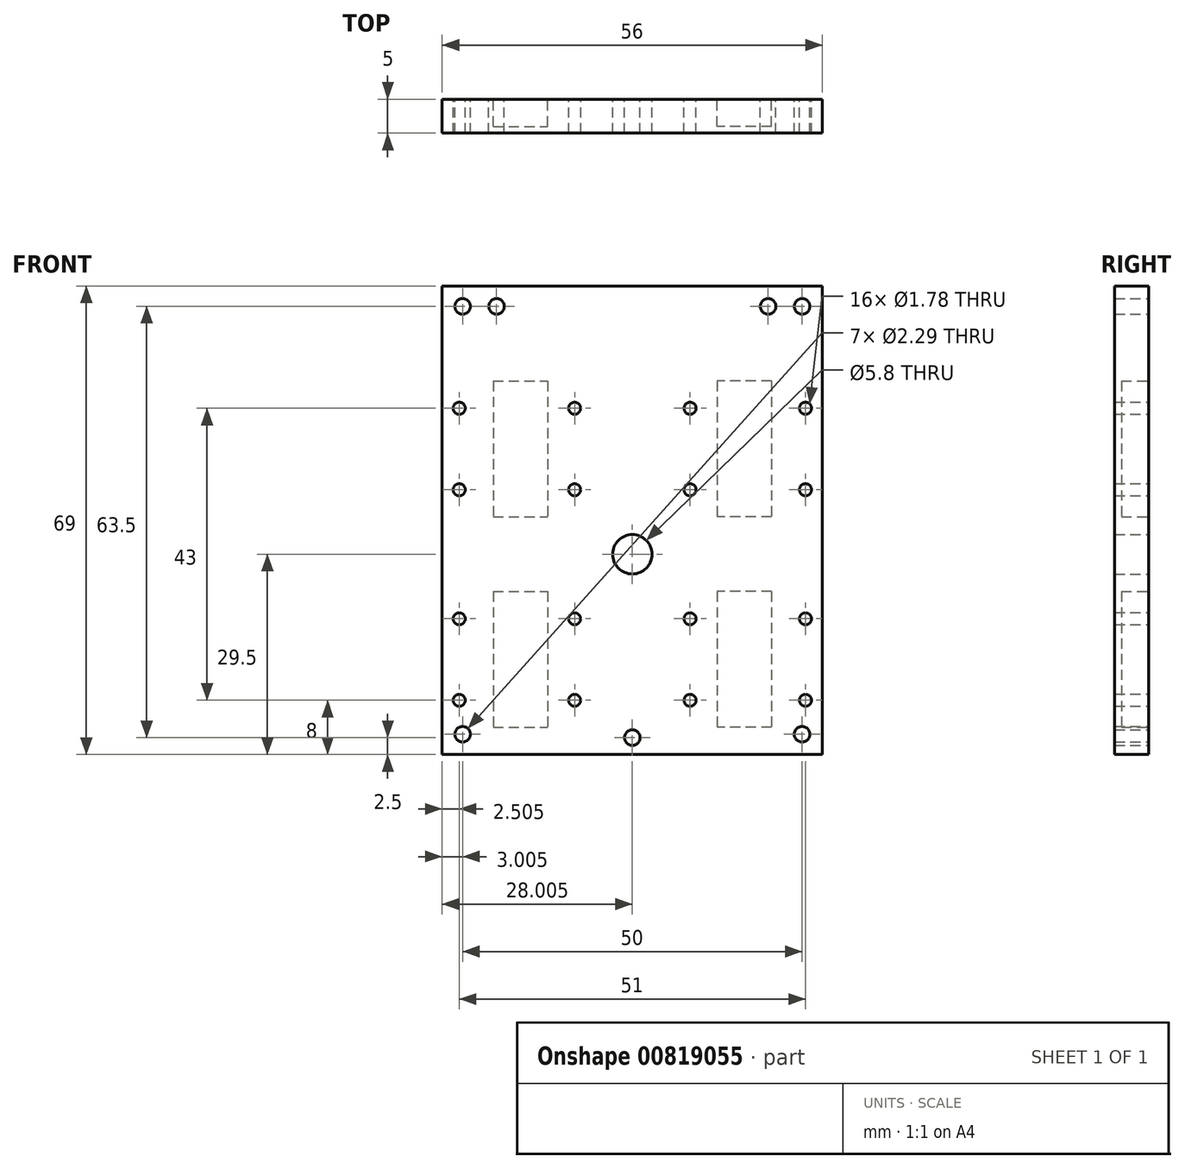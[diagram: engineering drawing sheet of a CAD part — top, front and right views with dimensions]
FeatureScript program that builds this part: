
annotation { "Feature Type Name" : "Feature", "Feature Type Description" : "" }
export const myFeature = defineFeature(function(context is Context, id is Id, definition is map)
    precondition{}
    {
        {
            var Q0;
            Q0=qCreatedBy(makeId("Front.planeOp"),FACE);
            var sketch = newSketch(context, id + "F0", { "sketchPlane" : qUnion([Q0])});
            skCircle(sketch, "E0", {"center": v(-20.38, 33.5) * mm, "radius": 1.14 * mm});
            skCircle(sketch, "E1", {"center": v(-25.88, 18.5) * mm, "radius": 0.89 * mm});
            skCircle(sketch, "E2", {"center": v(-8.88, 18.5) * mm, "radius": 0.89 * mm});
            skCircle(sketch, "E3", {"center": v(-8.88, 6.5) * mm, "radius": 0.89 * mm});
            skCircle(sketch, "E4", {"center": v(-25.88, 6.5) * mm, "radius": 0.89 * mm});
            skCircle(sketch, "E5", {"center": v(-25.87, -12.5) * mm, "radius": 0.89 * mm});
            skCircle(sketch, "E6", {"center": v(-8.88, -12.5) * mm, "radius": 0.89 * mm});
            skCircle(sketch, "E7", {"center": v(-8.88, -24.5) * mm, "radius": 0.89 * mm});
            skCircle(sketch, "E8", {"center": v(-25.87, -24.5) * mm, "radius": 0.89 * mm});
            skCircle(sketch, "E9", {"center": v(-25.38, -29.5) * mm, "radius": 1.14 * mm});
            skCircle(sketch, "E10", {"center": v(-0.38, -30) * mm, "radius": 1.14 * mm});
            skCircle(sketch, "E11", {"center": v(-0.38, -3) * mm, "radius": 2.9 * mm});
            skLineSegment(sketch, "E12", {"start": v(27.62, 36.5) * mm, "end": v(-28.38, 36.5) * mm});
            skLineSegment(sketch, "E13", {"start": v(-28.37, 36.5) * mm, "end": v(-28.38, -32.5) * mm});
            skLineSegment(sketch, "E14", {"start": v(27.63, -32.5) * mm, "end": v(-28.38, -32.5) * mm});
            skLineSegment(sketch, "E15.bottom", {"start": v(-28.38, -32.5) * mm, "end": v(-22.38, -32.5) * mm, "construction": true});
            skLineSegment(sketch, "E15.top", {"start": v(-28.38, -26.5) * mm, "end": v(-22.38, -26.5) * mm, "construction": true});
            skLineSegment(sketch, "E15.left", {"start": v(-28.38, -32.5) * mm, "end": v(-28.38, -26.5) * mm, "construction": true});
            skLineSegment(sketch, "E15.right", {"start": v(-22.38, -32.5) * mm, "end": v(-22.38, -26.5) * mm, "construction": true});
            skLineSegment(sketch, "E16", {"start": v(-28.38, -26.5) * mm, "end": v(-22.38, -32.5) * mm});
            skLineSegment(sketch, "E17", {"start": v(-28.38, -32.5) * mm, "end": v(-22.38, -26.5) * mm});
            skPoint(sketch, "E18", {"position": v(-28.38, 2) * mm});
            skLineSegment(sketch, "E19", {"start": v(-0.38, 36.5) * mm, "end": v(-20.38, 36.5) * mm, "construction": true});
            skLineSegment(sketch, "E20", {"start": v(-20.38, 36.5) * mm, "end": v(-20.38, 33.5) * mm});
            skLineSegment(sketch, "E21", {"start": v(-0.37, -32.5) * mm, "end": v(-0.38, -30) * mm});
            skLineSegment(sketch, "E22", {"start": v(-8.88, -12.5) * mm, "end": v(-8.88, -24.5) * mm, "construction": true});
            skPoint(sketch, "E23", {"position": v(-8.88, -18.5) * mm});
            skLineSegment(sketch, "E24", {"start": v(-8.88, -18.5) * mm, "end": v(-28.37, -18.5) * mm, "construction": true});
            skLineSegment(sketch, "E25", {"start": v(-25.88, -24.5) * mm, "end": v(-25.88, -12.5) * mm, "construction": true});
            skPoint(sketch, "E26", {"position": v(-25.88, -18.5) * mm});
            skPoint(sketch, "E27", {"position": v(-20.88, -18.5) * mm});
            skLineSegment(sketch, "E28", {"start": v(-20.88, -18.5) * mm, "end": v(-20.88, -8.5) * mm, "construction": true});
            skLineSegment(sketch, "E29", {"start": v(-20.88, -8.5) * mm, "end": v(-12.88, -8.5) * mm, "construction": true});
            skLineSegment(sketch, "E30", {"start": v(-12.88, -8.5) * mm, "end": v(-12.88, -28.5) * mm, "construction": true});
            skLineSegment(sketch, "E31.bottom", {"start": v(-20.88, -8.5) * mm, "end": v(-12.88, -8.5) * mm});
            skLineSegment(sketch, "E31.top", {"start": v(-20.88, -28.5) * mm, "end": v(-12.88, -28.5) * mm});
            skLineSegment(sketch, "E31.left", {"start": v(-20.88, -8.5) * mm, "end": v(-20.88, -28.5) * mm});
            skLineSegment(sketch, "E31.right", {"start": v(-12.88, -8.5) * mm, "end": v(-12.88, -28.5) * mm});
            skLineSegment(sketch, "E32", {"start": v(-25.88, 18.5) * mm, "end": v(-25.88, 6.5) * mm, "construction": true});
            skPoint(sketch, "E33", {"position": v(-25.88, 12.5) * mm});
            skLineSegment(sketch, "E34", {"start": v(-8.88, 18.5) * mm, "end": v(-8.88, 6.5) * mm, "construction": true});
            skPoint(sketch, "E35", {"position": v(-8.88, 12.5) * mm});
            skLineSegment(sketch, "E36", {"start": v(-8.88, 12.5) * mm, "end": v(-28.38, 12.5) * mm, "construction": true});
            skLineSegment(sketch, "E37", {"start": v(-25.88, 18.5) * mm, "end": v(-28.38, 18.5) * mm, "construction": true});
            skLineSegment(sketch, "E38", {"start": v(-25.87, -12.5) * mm, "end": v(-28.37, -12.5) * mm, "construction": true});
            skLineSegment(sketch, "E39", {"start": v(-20.88, -8.5) * mm, "end": v(-28.37, -8.5) * mm, "construction": true});
            skLineSegment(sketch, "E40", {"start": v(-28.38, 22.5) * mm, "end": v(-20.88, 22.5) * mm, "construction": true});
            skLineSegment(sketch, "E41", {"start": v(-20.88, 22.5) * mm, "end": v(-20.88, 12.5) * mm});
            skLineSegment(sketch, "E42", {"start": v(-20.88, 22.5) * mm, "end": v(-12.88, 22.5) * mm});
            skLineSegment(sketch, "E43", {"start": v(-12.88, 22.5) * mm, "end": v(-12.87, 2.5) * mm, "construction": true});
            skLineSegment(sketch, "E44.bottom", {"start": v(-20.88, 22.5) * mm, "end": v(-12.88, 22.5) * mm, "construction": true});
            skLineSegment(sketch, "E44.top", {"start": v(-20.88, 2.5) * mm, "end": v(-12.88, 2.5) * mm});
            skLineSegment(sketch, "E44.left", {"start": v(-20.88, 22.5) * mm, "end": v(-20.88, 2.5) * mm});
            skLineSegment(sketch, "E44.right", {"start": v(-12.87, 22.5) * mm, "end": v(-12.87, 2.5) * mm});
            skLineSegment(sketch, "E45", {"start": v(27.62, 36.5) * mm, "end": v(27.63, -32.5) * mm});
            skLineSegment(sketch, "E46", {"start": v(-0.38, -3) * mm, "end": v(-0.37, -30) * mm});
            skLineSegment(sketch, "E47", {"start": v(-0.38, 36.5) * mm, "end": v(-0.38, -3) * mm, "construction": true});
            skLineSegment(sketch, "E48.bottom", {"start": v(-28.38, 36.5) * mm, "end": v(-22.38, 36.5) * mm, "construction": true});
            skLineSegment(sketch, "E48.top", {"start": v(-28.38, 30.5) * mm, "end": v(-22.38, 30.5) * mm, "construction": true});
            skLineSegment(sketch, "E48.left", {"start": v(-28.38, 36.5) * mm, "end": v(-28.38, 30.5) * mm, "construction": true});
            skLineSegment(sketch, "E48.right", {"start": v(-22.38, 36.5) * mm, "end": v(-22.38, 30.5) * mm, "construction": true});
            skLineSegment(sketch, "E49", {"start": v(-28.38, 36.5) * mm, "end": v(-22.38, 30.5) * mm, "construction": true});
            skLineSegment(sketch, "E50", {"start": v(-28.38, 30.5) * mm, "end": v(-22.38, 36.5) * mm, "construction": true});
            skCircle(sketch, "E51", {"center": v(-25.38, 33.5) * mm, "radius": 1.14 * mm});
            skCircle(sketch, "E52.MirrorC", {"center": v(24.62, -29.5) * mm, "radius": 1.14 * mm});
            skCircle(sketch, "E53.MirrorC", {"center": v(25.12, -24.5) * mm, "radius": 0.89 * mm});
            skLineSegment(sketch, "E54.MirrorCS", {"start": v(12.12, -8.5) * mm, "end": v(12.13, -28.5) * mm});
            skLineSegment(sketch, "E55.MirrorCS", {"start": v(20.12, -8.5) * mm, "end": v(12.12, -8.5) * mm});
            skLineSegment(sketch, "E56.MirrorCS", {"start": v(20.12, -8.5) * mm, "end": v(20.12, -28.5) * mm});
            skPoint(sketch, "E57.MirrorP", {"position": v(20.12, -18.5) * mm});
            skLineSegment(sketch, "E58.MirrorCS", {"start": v(20.12, -8.5) * mm, "end": v(12.12, -8.5) * mm, "construction": true});
            skLineSegment(sketch, "E59.MirrorCS", {"start": v(8.12, -12.5) * mm, "end": v(8.13, -24.5) * mm, "construction": true});
            skLineSegment(sketch, "E60.MirrorCS", {"start": v(20.12, -28.5) * mm, "end": v(12.12, -28.5) * mm});
            skLineSegment(sketch, "E61.MirrorCS", {"start": v(20.12, -18.5) * mm, "end": v(20.12, -8.5) * mm, "construction": true});
            skCircle(sketch, "E62.MirrorC", {"center": v(8.13, -24.5) * mm, "radius": 0.89 * mm});
            skCircle(sketch, "E63.MirrorC", {"center": v(8.13, -12.5) * mm, "radius": 0.89 * mm});
            skPoint(sketch, "E64.MirrorP", {"position": v(25.12, -18.5) * mm});
            skPoint(sketch, "E65.MirrorP", {"position": v(8.12, -18.5) * mm});
            skCircle(sketch, "E66.MirrorC", {"center": v(25.12, -12.5) * mm, "radius": 0.89 * mm});
            skLineSegment(sketch, "E67.MirrorCS", {"start": v(25.12, -24.5) * mm, "end": v(25.13, -12.5) * mm, "construction": true});
            skLineSegment(sketch, "E68.MirrorCS", {"start": v(12.12, -8.5) * mm, "end": v(12.13, -28.5) * mm, "construction": true});
            skPoint(sketch, "E69.MirrorP", {"position": v(27.62, 2) * mm});
            skLineSegment(sketch, "E70.MirrorCS", {"start": v(12.12, 22.5) * mm, "end": v(12.12, 2.5) * mm});
            skLineSegment(sketch, "E71.MirrorCS", {"start": v(20.13, 22.5) * mm, "end": v(12.13, 22.5) * mm});
            skCircle(sketch, "E72.MirrorC", {"center": v(25.13, 18.5) * mm, "radius": 0.89 * mm});
            skLineSegment(sketch, "E73.MirrorCS", {"start": v(20.13, 22.5) * mm, "end": v(12.13, 22.5) * mm, "construction": true});
            skLineSegment(sketch, "E74.MirrorCS", {"start": v(20.13, 2.5) * mm, "end": v(12.13, 2.5) * mm});
            skPoint(sketch, "E75.MirrorP", {"position": v(25.13, 12.5) * mm});
            skLineSegment(sketch, "E76.MirrorCS", {"start": v(20.12, 22.5) * mm, "end": v(20.12, 2.5) * mm});
            skCircle(sketch, "E77.MirrorC", {"center": v(8.13, 18.5) * mm, "radius": 0.89 * mm});
            skLineSegment(sketch, "E78.MirrorCS", {"start": v(8.13, 18.5) * mm, "end": v(8.13, 6.5) * mm, "construction": true});
            skLineSegment(sketch, "E79.MirrorCS", {"start": v(12.12, 22.5) * mm, "end": v(12.12, 2.5) * mm, "construction": true});
            skLineSegment(sketch, "E80.MirrorCS", {"start": v(25.13, 18.5) * mm, "end": v(25.13, 6.5) * mm, "construction": true});
            skLineSegment(sketch, "E81.MirrorCS", {"start": v(20.13, 22.5) * mm, "end": v(20.13, 12.5) * mm});
            skCircle(sketch, "E82.MirrorC", {"center": v(25.13, 6.5) * mm, "radius": 0.89 * mm});
            skCircle(sketch, "E83.MirrorC", {"center": v(8.13, 6.5) * mm, "radius": 0.89 * mm});
            skPoint(sketch, "E84.MirrorP", {"position": v(8.13, 12.5) * mm});
            skCircle(sketch, "E85.MirrorC", {"center": v(24.63, 33.5) * mm, "radius": 1.14 * mm});
            skCircle(sketch, "E86.MirrorC", {"center": v(19.63, 33.5) * mm, "radius": 1.14 * mm});
            skSolve(sketch);
        }
        {
            var Q0;
            Q0=qCreatedBy(makeId("Front.planeOp"),FACE);
            var sketch = newSketch(context, id + "F1", { "sketchPlane" : qUnion([Q0])});
            skLineSegment(sketch, "E87.0", {"start": v(27.62, 36.5) * mm, "end": v(-28.38, 36.5) * mm});
            skLineSegment(sketch, "E87.1", {"start": v(-28.37, 36.5) * mm, "end": v(-28.38, -32.5) * mm});
            skLineSegment(sketch, "E87.2", {"start": v(27.62, 36.5) * mm, "end": v(27.63, -32.5) * mm});
            skLineSegment(sketch, "E87.3", {"start": v(27.63, -32.5) * mm, "end": v(-28.38, -32.5) * mm});
            skSolve(sketch);
        }
        {
            var Q0;
            Q0=qCreatedBy(makeId("Front.planeOp"),FACE);
            var sketch = newSketch(context, id + "F2", { "sketchPlane" : qUnion([Q0])});
            skLineSegment(sketch, "E88.0", {"start": v(-20.88, 2.5) * mm, "end": v(-12.88, 2.5) * mm});
            skLineSegment(sketch, "E88.1", {"start": v(-12.87, 22.5) * mm, "end": v(-12.87, 2.5) * mm});
            skLineSegment(sketch, "E88.2", {"start": v(-20.88, 22.5) * mm, "end": v(-12.88, 22.5) * mm});
            skLineSegment(sketch, "E88.3", {"start": v(-20.88, 22.5) * mm, "end": v(-20.88, 12.5) * mm});
            skLineSegment(sketch, "E88.4", {"start": v(-20.88, -8.5) * mm, "end": v(-12.88, -8.5) * mm});
            skLineSegment(sketch, "E88.5", {"start": v(-20.88, -8.5) * mm, "end": v(-20.88, -28.5) * mm});
            skLineSegment(sketch, "E88.6", {"start": v(-12.88, -8.5) * mm, "end": v(-12.88, -28.5) * mm});
            skLineSegment(sketch, "E88.7", {"start": v(-20.88, -28.5) * mm, "end": v(-12.88, -28.5) * mm});
            skLineSegment(sketch, "E88.17", {"start": v(-20.88, 22.5) * mm, "end": v(-20.88, 2.5) * mm});
            skLineSegment(sketch, "E89.0", {"start": v(20.13, 22.5) * mm, "end": v(12.13, 22.5) * mm});
            skLineSegment(sketch, "E89.1", {"start": v(12.12, 22.5) * mm, "end": v(12.12, 2.5) * mm});
            skLineSegment(sketch, "E89.2", {"start": v(20.13, 22.5) * mm, "end": v(20.13, 12.5) * mm});
            skLineSegment(sketch, "E89.3", {"start": v(20.12, 22.5) * mm, "end": v(20.12, 2.5) * mm});
            skLineSegment(sketch, "E89.4", {"start": v(20.13, 2.5) * mm, "end": v(12.13, 2.5) * mm});
            skLineSegment(sketch, "E89.5", {"start": v(20.12, -8.5) * mm, "end": v(20.12, -28.5) * mm});
            skLineSegment(sketch, "E89.6", {"start": v(20.12, -8.5) * mm, "end": v(12.12, -8.5) * mm});
            skLineSegment(sketch, "E89.7", {"start": v(12.12, -8.5) * mm, "end": v(12.13, -28.5) * mm});
            skLineSegment(sketch, "E89.8", {"start": v(20.12, -28.5) * mm, "end": v(12.12, -28.5) * mm});
            skSolve(sketch);
        }
        {
            var Q0;
            Q0=qCreatedBy(makeId("Front.planeOp"),FACE);
            var sketch = newSketch(context, id + "F3", { "sketchPlane" : qUnion([Q0])});
            skCircle(sketch, "E90.0", {"center": v(-25.88, 18.5) * mm, "radius": 0.89 * mm});
            skCircle(sketch, "E90.1", {"center": v(-25.88, 6.5) * mm, "radius": 0.89 * mm});
            skCircle(sketch, "E90.2", {"center": v(-8.88, 18.5) * mm, "radius": 0.89 * mm});
            skCircle(sketch, "E90.3", {"center": v(-8.88, 6.5) * mm, "radius": 0.89 * mm});
            skCircle(sketch, "E90.10", {"center": v(-8.88, -12.5) * mm, "radius": 0.89 * mm});
            skCircle(sketch, "E90.11", {"center": v(-25.87, -12.5) * mm, "radius": 0.89 * mm});
            skCircle(sketch, "E90.12", {"center": v(-25.87, -24.5) * mm, "radius": 0.89 * mm});
            skCircle(sketch, "E90.13", {"center": v(-8.88, -24.5) * mm, "radius": 0.89 * mm});
            skCircle(sketch, "E90.21", {"center": v(-0.38, -30) * mm, "radius": 1.14 * mm});
            skCircle(sketch, "E90.22", {"center": v(-25.38, -29.5) * mm, "radius": 1.14 * mm});
            skCircle(sketch, "E91.0", {"center": v(-0.38, -3) * mm, "radius": 2.9 * mm});
            skCircle(sketch, "E92.0", {"center": v(-25.38, 33.5) * mm, "radius": 1.14 * mm});
            skCircle(sketch, "E92.1", {"center": v(8.13, 18.5) * mm, "radius": 0.89 * mm});
            skCircle(sketch, "E92.2", {"center": v(8.13, 6.5) * mm, "radius": 0.89 * mm});
            skCircle(sketch, "E92.3", {"center": v(25.13, 18.5) * mm, "radius": 0.89 * mm});
            skCircle(sketch, "E92.4", {"center": v(24.63, 33.5) * mm, "radius": 1.14 * mm});
            skCircle(sketch, "E92.5", {"center": v(8.13, -12.5) * mm, "radius": 0.89 * mm});
            skCircle(sketch, "E92.6", {"center": v(8.13, -24.5) * mm, "radius": 0.89 * mm});
            skCircle(sketch, "E92.7", {"center": v(25.12, -12.5) * mm, "radius": 0.89 * mm});
            skCircle(sketch, "E92.8", {"center": v(25.12, -24.5) * mm, "radius": 0.89 * mm});
            skCircle(sketch, "E92.9", {"center": v(24.62, -29.5) * mm, "radius": 1.14 * mm});
            skCircle(sketch, "E92.10", {"center": v(25.13, 6.5) * mm, "radius": 0.89 * mm});
            skCircle(sketch, "E93.0", {"center": v(-20.38, 33.5) * mm, "radius": 1.14 * mm});
            skCircle(sketch, "E93.1", {"center": v(19.63, 33.5) * mm, "radius": 1.14 * mm});
            skSolve(sketch);
        }
        {
            var Q0;
            Q0 = qSketchRegion(id + "F1", true);
            extrude(context, id + "F4", {"entities" : qUnion([Q0]), "depth" : 5 * mm, "offsetDistance" : 25 * mm});
        }
        {
            var Q0;
            {Q0=qUnion([makeQuery(id+"F2.imprint","IMPRINT",FACE,{"disambiguationData":[TD([[makeQuery(id+"F2.imprint","IMPRINT",EDGE,{"derivedFrom":sQuery(id+"F2.wireOp",EDGE,"E88.0")}),1.0]])]}),makeQuery(id+"F2.imprint","IMPRINT",FACE,{"disambiguationData":[TD([[makeQuery(id+"F2.imprint","IMPRINT",EDGE,{"derivedFrom":sQuery(id+"F2.wireOp",EDGE,"E88.4")}),-1.0]])]}),makeQuery(id+"F2.imprint","IMPRINT",FACE,{"disambiguationData":[TD([[makeQuery(id+"F2.imprint","IMPRINT",EDGE,{"derivedFrom":sQuery(id+"F2.wireOp",EDGE,"E89.0")}),1.0]])]}),makeQuery(id+"F2.imprint","IMPRINT",FACE,{"disambiguationData":[TD([[makeQuery(id+"F2.imprint","IMPRINT",EDGE,{"derivedFrom":sQuery(id+"F2.wireOp",EDGE,"E89.5")}),-1.0]])]})]);}
            extrude(context, id + "F5", {"entities" : qUnion([Q0]), "operationType" : NewBodyOperationType.REMOVE, "depth" : 4 * mm, "offsetDistance" : 25 * mm});
        }
        {
            var Q0;
            Q0 = qSketchRegion(id + "F3", true);
            extrude(context, id + "F6", {"entities" : qUnion([Q0]), "operationType" : NewBodyOperationType.REMOVE, "endBound" : BoundingType.THROUGH_ALL, "depth" : 25 * mm, "offsetDistance" : 25 * mm});
        }
    });
